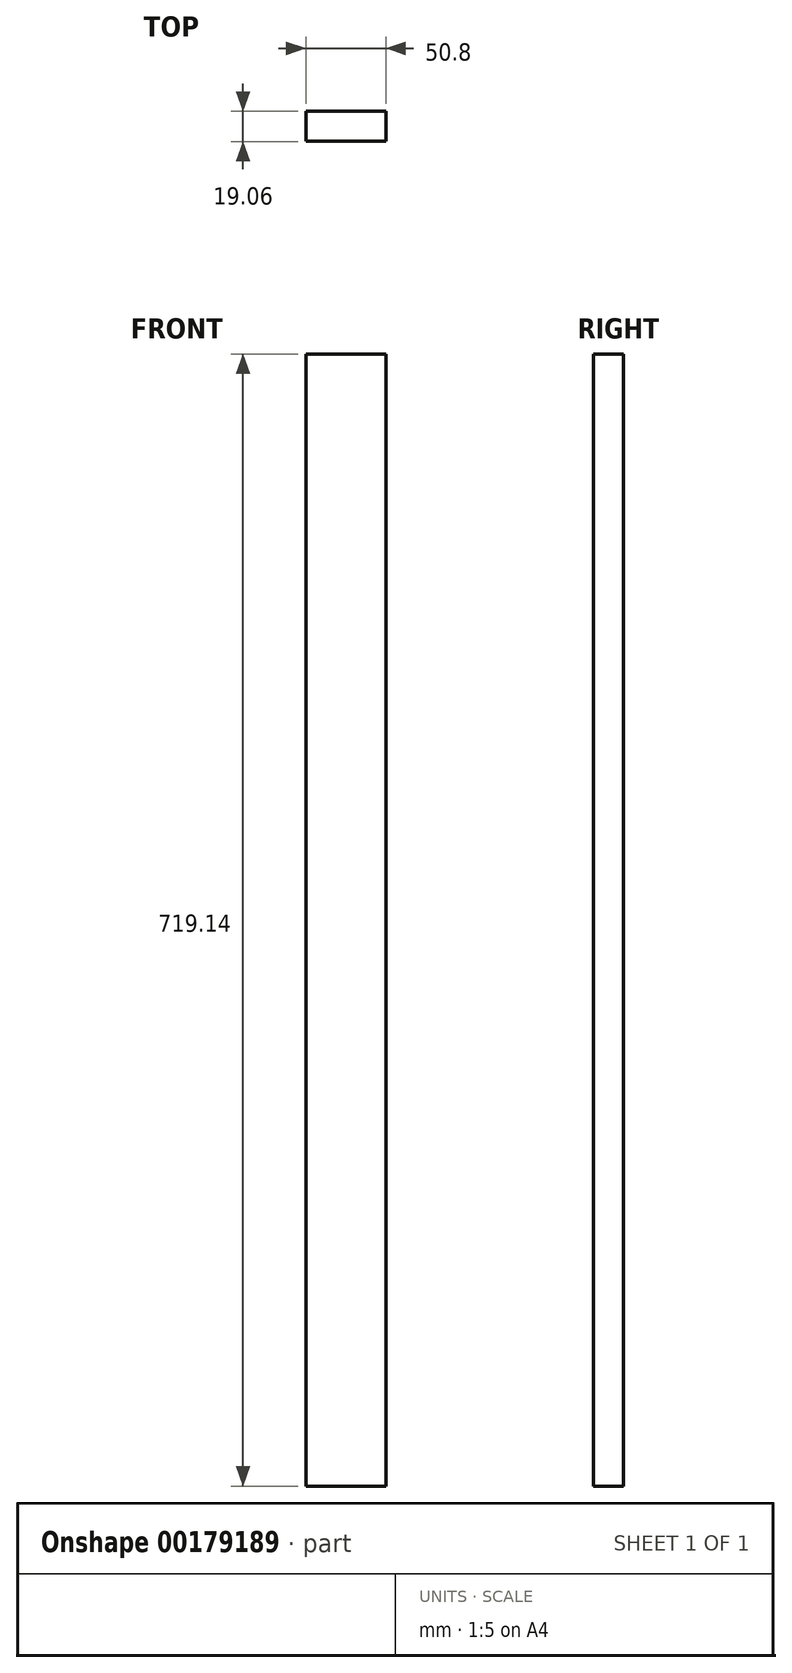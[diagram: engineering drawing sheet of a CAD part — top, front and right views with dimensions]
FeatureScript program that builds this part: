
annotation { "Feature Type Name" : "Feature", "Feature Type Description" : "" }
export const myFeature = defineFeature(function(context is Context, id is Id, definition is map)
    precondition{}
    {
        {
            var Q0;
            Q0=qCreatedBy(makeId("Front.planeOp"),FACE);
            var sketch = newSketch(context, id + "F0", { "sketchPlane" : qUnion([Q0])});
            skLineSegment(sketch, "E0.bottom", {"start": v(-44.7, 359.57) * mm, "end": v(6.1, 359.57) * mm});
            skLineSegment(sketch, "E0.top", {"start": v(-44.7, -359.57) * mm, "end": v(6.1, -359.57) * mm});
            skLineSegment(sketch, "E0.left", {"start": v(-44.7, 359.57) * mm, "end": v(-44.7, -359.57) * mm});
            skLineSegment(sketch, "E0.right", {"start": v(6.1, 359.57) * mm, "end": v(6.1, -359.57) * mm});
            skLineSegment(sketch, "E1", {"start": v(-44.7, 0) * mm, "end": v(6.1, 0) * mm});
            skSolve(sketch);
        }
        {
            var Q0;
            {var subQ0=sQuery(id+"F0.wireOp",EDGE,"E0.bottom");Q0=makeQuery(id+"F0.imprint","IMPRINT",FACE,{"disambiguationData":[TD([[makeQuery(id+"F0.imprint","IMPRINT",EDGE,{"derivedFrom":subQ0}),-1.0]])]});}
            var Q1;
            {var subQ0=sQuery(id+"F0.wireOp",EDGE,"E0.top");Q1=makeQuery(id+"F0.imprint","IMPRINT",FACE,{"disambiguationData":[TD([[makeQuery(id+"F0.imprint","IMPRINT",EDGE,{"derivedFrom":subQ0}),1.0]])]});}
            extrude(context, id + "F1", {"entities" : qUnion([Q0, Q1]), "depth" : 19.05 * mm, "symmetric" : true});
        }
    });
